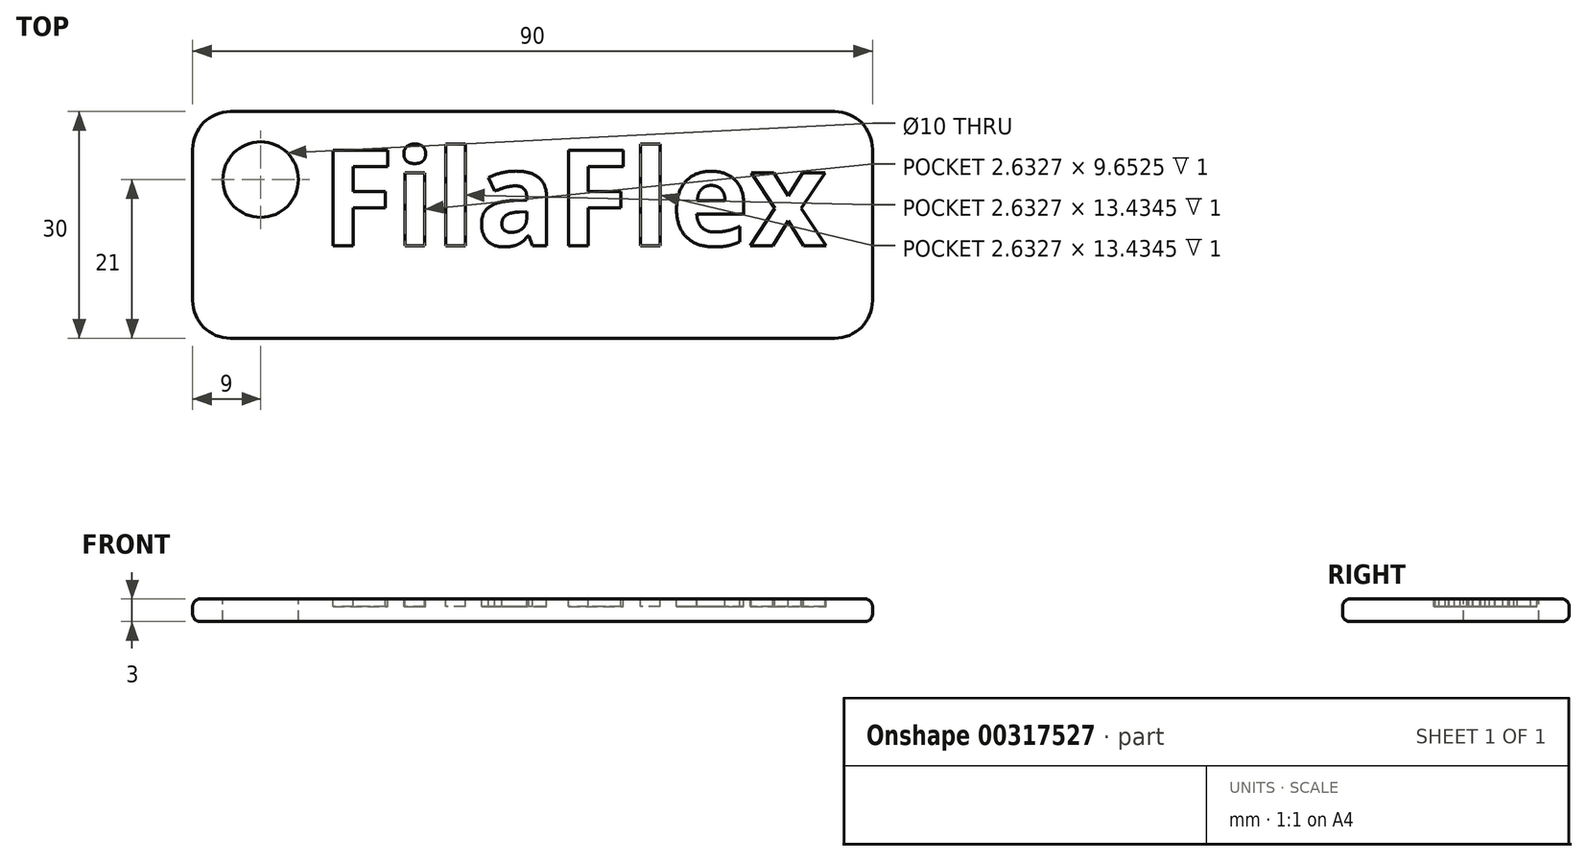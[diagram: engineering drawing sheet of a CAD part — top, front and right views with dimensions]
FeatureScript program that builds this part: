
annotation { "Feature Type Name" : "Feature", "Feature Type Description" : "" }
export const myFeature = defineFeature(function(context is Context, id is Id, definition is map)
    precondition{}
    {
        {
            var Q0;
            Q0=qCreatedBy(makeId("Top.planeOp"),FACE);
            var sketch = newSketch(context, id + "F0", { "sketchPlane" : qUnion([Q0])});
            skLineSegment(sketch, "E0.bottom", {"start": v(-45, 15) * mm, "end": v(45, 15) * mm});
            skLineSegment(sketch, "E0.top", {"start": v(-45, -15) * mm, "end": v(45, -15) * mm});
            skLineSegment(sketch, "E0.left", {"start": v(-45, 15) * mm, "end": v(-45, -15) * mm});
            skLineSegment(sketch, "E0.right", {"start": v(45, 15) * mm, "end": v(45, -15) * mm});
            skLineSegment(sketch, "E1", {"start": v(-45, 15) * mm, "end": v(45, -15) * mm, "construction": true});
            skSolve(sketch);
        }
        {
            var Q0;
            Q0=makeQuery(id+"F0.imprint","IMPRINT",FACE,{"disambiguationData":[TD([[makeQuery(id+"F0.imprint","IMPRINT",EDGE,{"derivedFrom":sQuery(id+"F0.wireOp",EDGE,"E0.bottom")}),-1.0]])]});
            extrude(context, id + "F1", {"entities" : qUnion([Q0]), "depth" : 3 * mm});
        }
        {
            var Q0;
            Q0=makeQuery(id+"F1.opExtrude","CAP_FACE",FACE,{"disambiguationData":[OSD([sQuery(id+"F0.wireOp",EDGE,"E0.bottom"),sQuery(id+"F0.wireOp",EDGE,"E0.top"),sQuery(id+"F0.wireOp",EDGE,"E0.left"),sQuery(id+"F0.wireOp",EDGE,"E0.right")])],"isStart":false});
            var Q1;
            Q1=makeQuery(id+"F1.opExtrude","CAP_FACE",FACE,{"disambiguationData":[OSD([sQuery(id+"F0.wireOp",EDGE,"E0.bottom"),sQuery(id+"F0.wireOp",EDGE,"E0.top"),sQuery(id+"F0.wireOp",EDGE,"E0.left"),sQuery(id+"F0.wireOp",EDGE,"E0.right")])],"isStart":true});
            fillet(context, id + "F2", {"entities" : qUnion([Q0, Q1]), "radius" : 1 * mm, "tangentPropagation" : true, "allowEdgeOverflow" : false});
        }
        {
            var Q0;
            Q0=makeQuery(id+"F1.opExtrude","SWEPT_EDGE",EDGE,{"disambiguationData":[OSD([sQuery(id+"F0.wireOp",EDGE,"E0.top"),sQuery(id+"F0.wireOp",EDGE,"E0.right")])]});
            var Q1;
            Q1=makeQuery(id+"F1.opExtrude","SWEPT_EDGE",EDGE,{"disambiguationData":[OSD([sQuery(id+"F0.wireOp",EDGE,"E0.bottom"),sQuery(id+"F0.wireOp",EDGE,"E0.right")])]});
            var Q2;
            Q2=makeQuery(id+"F1.opExtrude","SWEPT_EDGE",EDGE,{"disambiguationData":[OSD([sQuery(id+"F0.wireOp",EDGE,"E0.bottom"),sQuery(id+"F0.wireOp",EDGE,"E0.left")])]});
            var Q3;
            Q3=makeQuery(id+"F1.opExtrude","SWEPT_EDGE",EDGE,{"disambiguationData":[OSD([sQuery(id+"F0.wireOp",EDGE,"E0.top"),sQuery(id+"F0.wireOp",EDGE,"E0.left")])]});
            fillet(context, id + "F3", {"entities" : qUnion([Q0, Q1, Q2, Q3]), "radius" : 5 * mm, "tangentPropagation" : true, "allowEdgeOverflow" : false});
        }
        {
            var Q0;
            {var subQ0=sQuery(id+"F0.wireOp",EDGE,"E0.left");var subQ2=sQuery(id+"F0.wireOp",EDGE,"E0.bottom");var subQ4=sQuery(id+"F0.wireOp",EDGE,"E0.right");var subQ6=sQuery(id+"F0.wireOp",EDGE,"E0.top");Q0=makeQuery(id+"FmQCBBX3Ub0qneL_1.boolean.opBoolean","SPLIT",FACE,{"disambiguationData":[TD([makeQuery(id+"FmQCBBX3Ub0qneL_1.opExtrude","SWEPT_FACE",FACE,{"disambiguationData":[OSD([sQuery(id+"FOCoeRmDbjhRCuz_1.wireOp",EDGE,"4a1fb44a-e7be-4e23-9449-000d953c446c.sketch_text.stroke-0")])]})])],"derivedFrom":makeQuery(id+"F1.opExtrude","CAP_FACE",FACE,{"disambiguationData":[OSD([subQ2,subQ6,subQ0,subQ4])],"isStart":false})});}
            var sketch = newSketch(context, id + "F4", { "sketchPlane" : qUnion([Q0])});
            skCircle(sketch, "E2", {"center": v(-36, 6) * mm, "radius": 5 * mm});
            skSolve(sketch);
        }
        {
            var Q0;
            Q0=qSketchRegion(id+"F4",true);
            extrude(context, id + "F5", {"entities" : qUnion([Q0]), "operationType" : NewBodyOperationType.REMOVE, "oppositeDirection" : true, "depth" : 3 * mm});
        }
        {
            var Q0;
            Q0=makeQuery(id+"F1.opExtrude","CAP_FACE",FACE,{"disambiguationData":[OSD([sQuery(id+"F0.wireOp",EDGE,"E0.bottom"),sQuery(id+"F0.wireOp",EDGE,"E0.top"),sQuery(id+"F0.wireOp",EDGE,"E0.left"),sQuery(id+"F0.wireOp",EDGE,"E0.right")])],"isStart":false});
            var sketch = newSketch(context, id + "F6", { "sketchPlane" : qUnion([Q0])});
            skText(sketch, "E3", { "text": "FilaFlex", "fontName": "OpenSans-Bold.ttf"});
            const initialGuessF6  = {"E3": [-0.028, -0.00273, 1, 0, 0.01273]};
            skSetInitialGuess(sketch, initialGuessF6);
            skSolve(sketch);
        }
        {
            var Q0;
            Q0=qSketchRegion(id+"F6",true);
            extrude(context, id + "F7", {"entities" : qUnion([Q0]), "operationType" : NewBodyOperationType.REMOVE, "oppositeDirection" : true, "depth" : 1 * mm});
        }
    });
